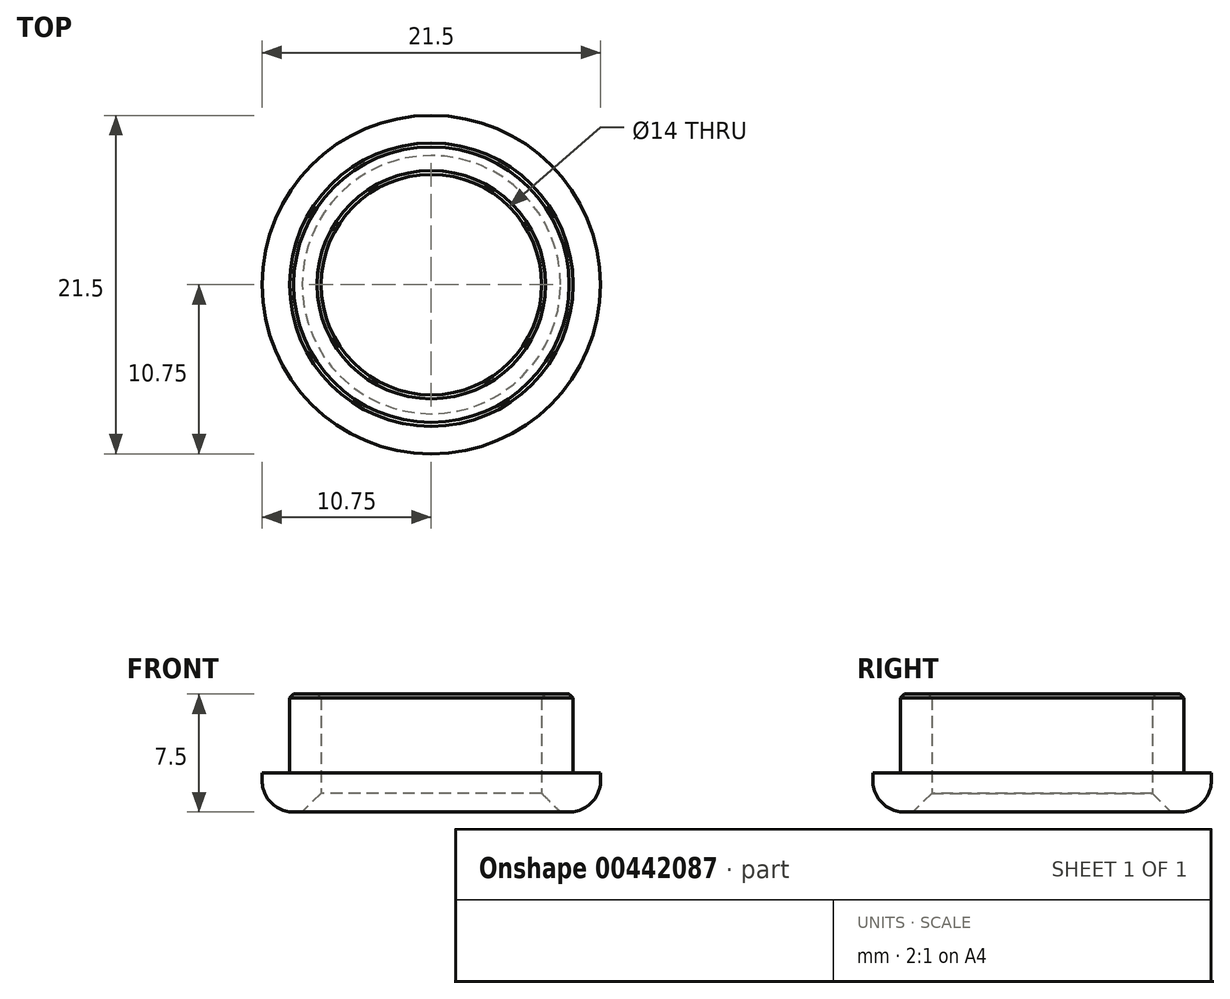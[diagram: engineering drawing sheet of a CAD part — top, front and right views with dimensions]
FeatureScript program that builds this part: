
annotation { "Feature Type Name" : "Feature", "Feature Type Description" : "" }
export const myFeature = defineFeature(function(context is Context, id is Id, definition is map)
    precondition{}
    {
        {
            var Q0;
            Q0=qCreatedBy(makeId("Top.planeOp"),FACE);
            var sketch = newSketch(context, id + "F0", { "sketchPlane" : qUnion([Q0])});
            skCircle(sketch, "E0", {"center": v(0, 0) * mm, "radius": 9 * mm});
            skCircle(sketch, "E1", {"center": v(0, 0) * mm, "radius": 7 * mm});
            skCircle(sketch, "E2", {"center": v(0, 0) * mm, "radius": 10.75 * mm});
            skSolve(sketch);
        }
        {
            var Q0;
            Q0=makeQuery(id+"F0.imprint","IMPRINT",FACE,{"disambiguationData":[TD([[makeQuery(id+"F0.imprint","IMPRINT",EDGE,{"derivedFrom":sQuery(id+"F0.wireOp",EDGE,"E0")}),1.0]])]});
            extrude(context, id + "F1", {"entities" : qUnion([Q0]), "depth" : 7.5 * mm});
        }
        {
            var Q0;
            Q0=makeQuery(id+"F0.imprint","IMPRINT",FACE,{"disambiguationData":[TD([[makeQuery(id+"F0.imprint","IMPRINT",EDGE,{"derivedFrom":sQuery(id+"F0.wireOp",EDGE,"E0")}),-1.0]])]});
            extrude(context, id + "F2", {"entities" : qUnion([Q0]), "operationType" : NewBodyOperationType.ADD, "depth" : 2.5 * mm});
        }
        {
            var Q0;
            Q0=makeQuery(id+"F1.opExtrude","CAP_EDGE",EDGE,{"disambiguationData":[OSD([sQuery(id+"F0.wireOp",EDGE,"E0")])],"isStart":false});
            var Q1;
            Q1=makeQuery(id+"F1.opExtrude","CAP_EDGE",EDGE,{"disambiguationData":[OSD([sQuery(id+"F0.wireOp",EDGE,"E1")])],"isStart":false});
            chamfer(context, id + "F3", {"entities" : qUnion([Q0, Q1]), "width" : 0.25 * mm, "tangentPropagation" : true});
        }
        {
            var Q0;
            Q0=makeQuery(id+"F2.opExtrude","CAP_EDGE",EDGE,{"disambiguationData":[OSD([sQuery(id+"F0.wireOp",EDGE,"E2")])],"isStart":true});
            fillet(context, id + "F4", {"entities" : qUnion([Q0]), "radius" : 2 * mm, "tangentPropagation" : true, "allowEdgeOverflow" : false});
        }
        {
            var Q0;
            Q0=makeQuery(id+"F1.opExtrude","CAP_EDGE",EDGE,{"disambiguationData":[OSD([sQuery(id+"F0.wireOp",EDGE,"E1")])],"isStart":true});
            chamfer(context, id + "F5", {"entities" : qUnion([Q0]), "width" : 1.2 * mm, "tangentPropagation" : true});
        }
    });
